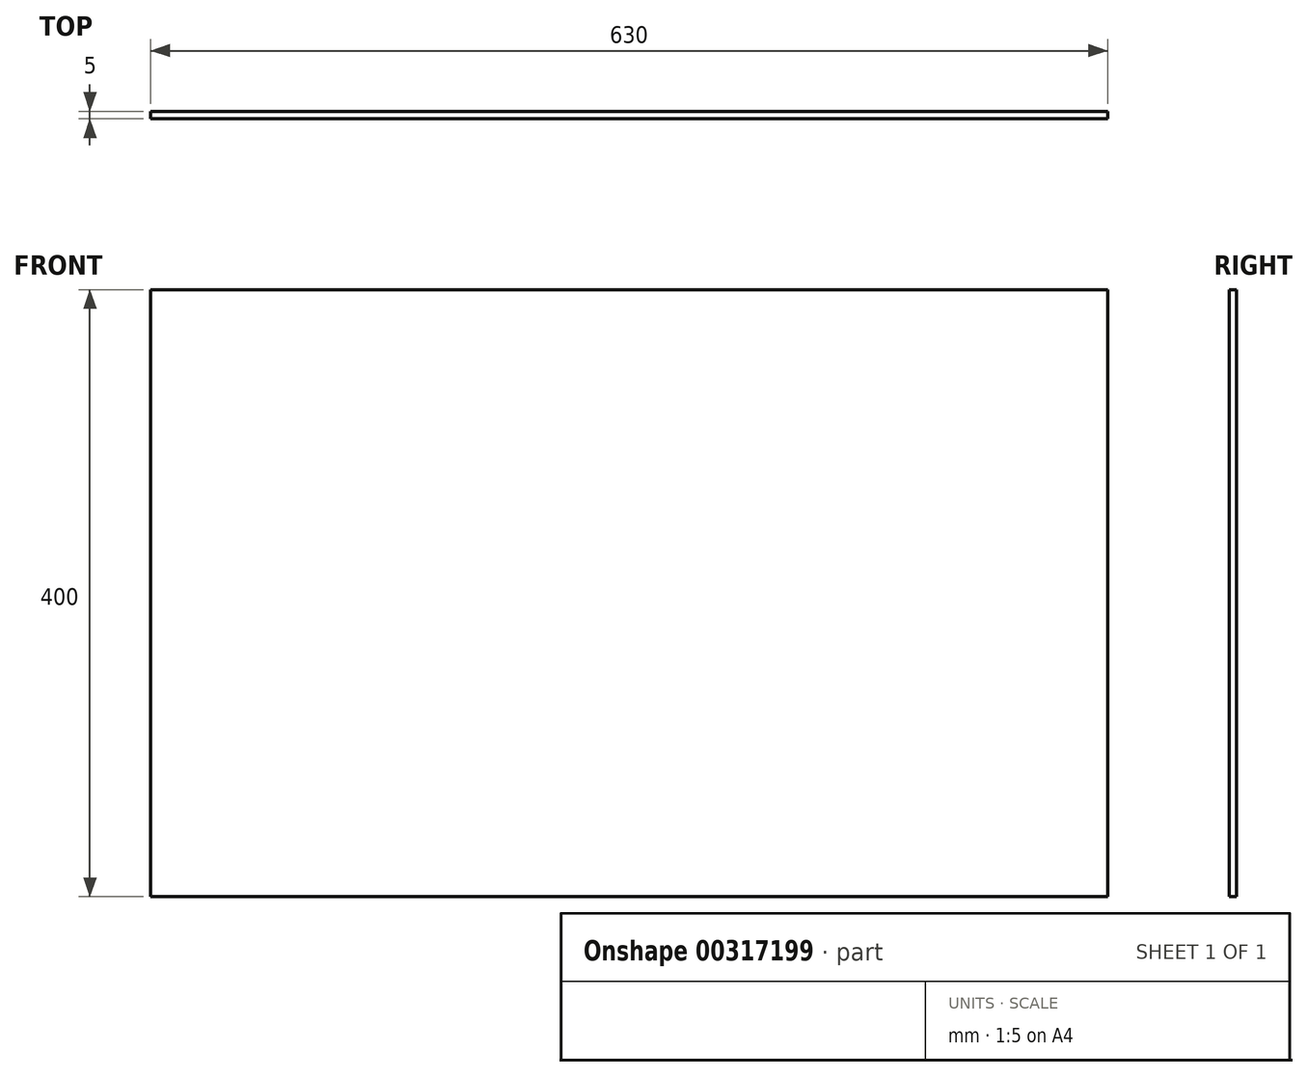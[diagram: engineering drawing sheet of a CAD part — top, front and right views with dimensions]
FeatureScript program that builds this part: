
annotation { "Feature Type Name" : "Feature", "Feature Type Description" : "" }
export const myFeature = defineFeature(function(context is Context, id is Id, definition is map)
    precondition{}
    {
        {
            var Q0;
            Q0=qCreatedBy(makeId("Front.planeOp"),FACE);
            var sketch = newSketch(context, id + "F0", { "sketchPlane" : qUnion([Q0])});
            skLineSegment(sketch, "E0.bottom", {"start": v(-315, 200) * mm, "end": v(315, 200) * mm});
            skLineSegment(sketch, "E0.top", {"start": v(-315, -200) * mm, "end": v(315, -200) * mm});
            skLineSegment(sketch, "E0.left", {"start": v(-315, 200) * mm, "end": v(-315, -200) * mm});
            skLineSegment(sketch, "E0.right", {"start": v(315, 200) * mm, "end": v(315, -200) * mm});
            skLineSegment(sketch, "E1", {"start": v(-315, 200) * mm, "end": v(315, -200) * mm, "construction": true});
            skSolve(sketch);
        }
        {
            var Q0;
            Q0 = qSketchRegion(id + "F0", true);
            extrude(context, id + "F1", {"entities" : qUnion([Q0]), "depth" : 5 * mm});
        }
    });
